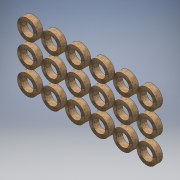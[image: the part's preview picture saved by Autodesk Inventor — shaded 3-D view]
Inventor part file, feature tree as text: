
AUTODESK INVENTOR PART (.ipt)
format: ipt  version: 2016 (Build 200138000, 138)  size: 228,864 bytes
history: native  units: mm
features: extrude x1, sketch x1
ambient origin geometry x8: Origin, YZ Plane, XZ Plane, XY Plane, X Axis, Y Axis, Z Axis, Center Point
bodies: Body1 (feature_tree)
feature tree (2):
  extrude  "Extrusion2"  Depth=3.0mm
  sketch  "Sketch1"  dims[d6=6.35mm d21=14.0mm d22=10.0mm d23=60.0mm d25=12.0mm d26=30.0mm d28=12.0mm d32=2.0mm d33=2.0mm d34=74.0mm d35=38.0mm d36=3.0mm d37=0.0mm]
